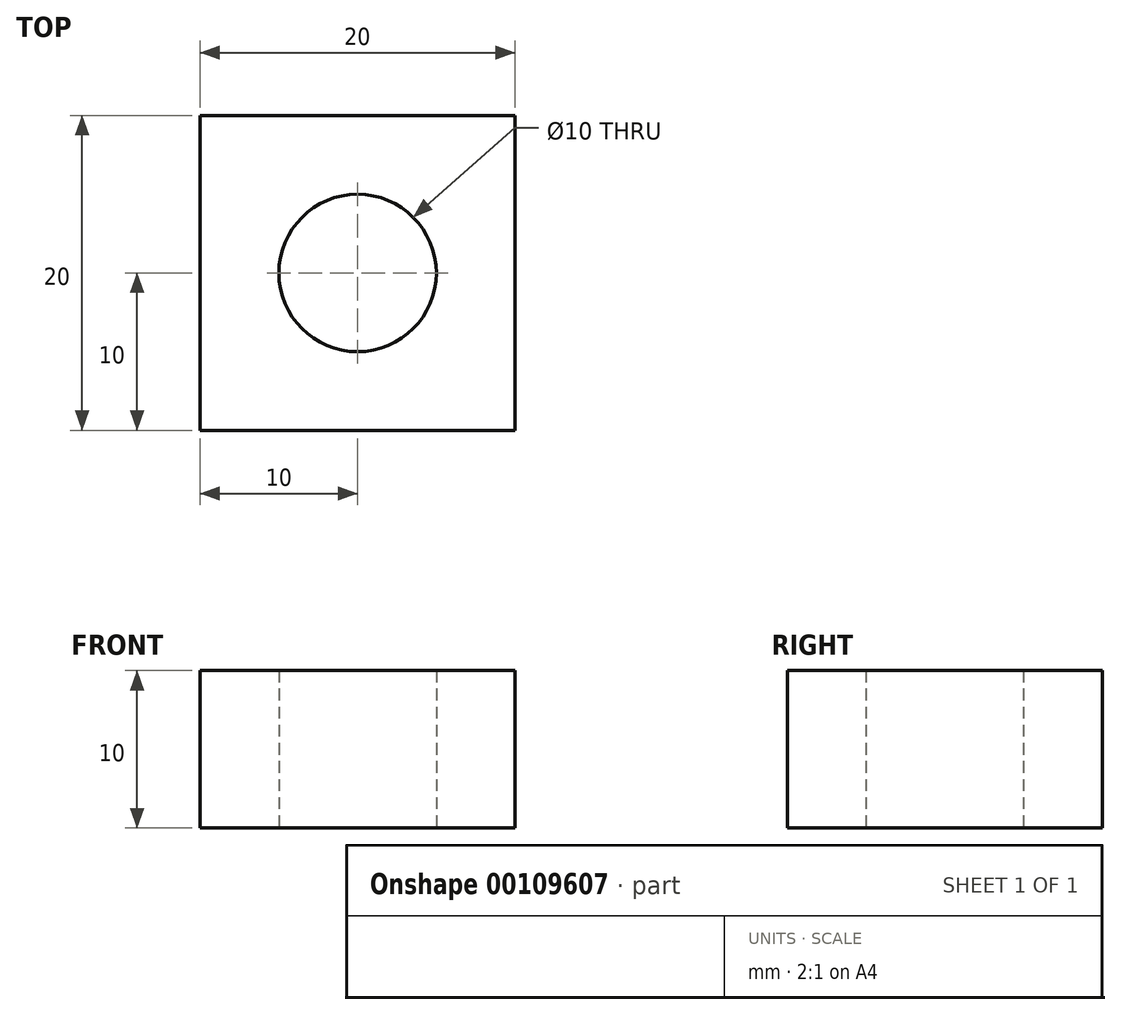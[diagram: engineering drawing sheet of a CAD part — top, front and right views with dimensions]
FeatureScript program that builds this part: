
annotation { "Feature Type Name" : "Feature", "Feature Type Description" : "" }
export const myFeature = defineFeature(function(context is Context, id is Id, definition is map)
    precondition{}
    {
        {
            var Q0;
            Q0=qCreatedBy(makeId("Top.planeOp"),FACE);
            var sketch = newSketch(context, id + "F0", { "sketchPlane" : qUnion([Q0])});
            skLineSegment(sketch, "E0.bottom", {"start": v(10, -10) * mm, "end": v(-10, -10) * mm});
            skLineSegment(sketch, "E0.top", {"start": v(10, 10) * mm, "end": v(-10, 10) * mm});
            skLineSegment(sketch, "E0.left", {"start": v(10, -10) * mm, "end": v(10, 10) * mm});
            skLineSegment(sketch, "E0.right", {"start": v(-10, -10) * mm, "end": v(-10, 10) * mm});
            skPoint(sketch, "E0.middle", {"position": v(0, 0) * mm});
            skCircle(sketch, "E1", {"center": v(0, 0) * mm, "radius": 5 * mm});
            skSolve(sketch);
        }
        {
            var Q0;
            Q0=makeQuery(id+"F0.imprint","IMPRINT",FACE,{"disambiguationData":[TD([[makeQuery(id+"F0.imprint","IMPRINT",EDGE,{"derivedFrom":sQuery(id+"F0.wireOp",EDGE,"E0.bottom")}),-1.0]])]});
            extrude(context, id + "F1", {"entities" : qUnion([Q0]), "depth" : 10 * mm});
        }
    });
